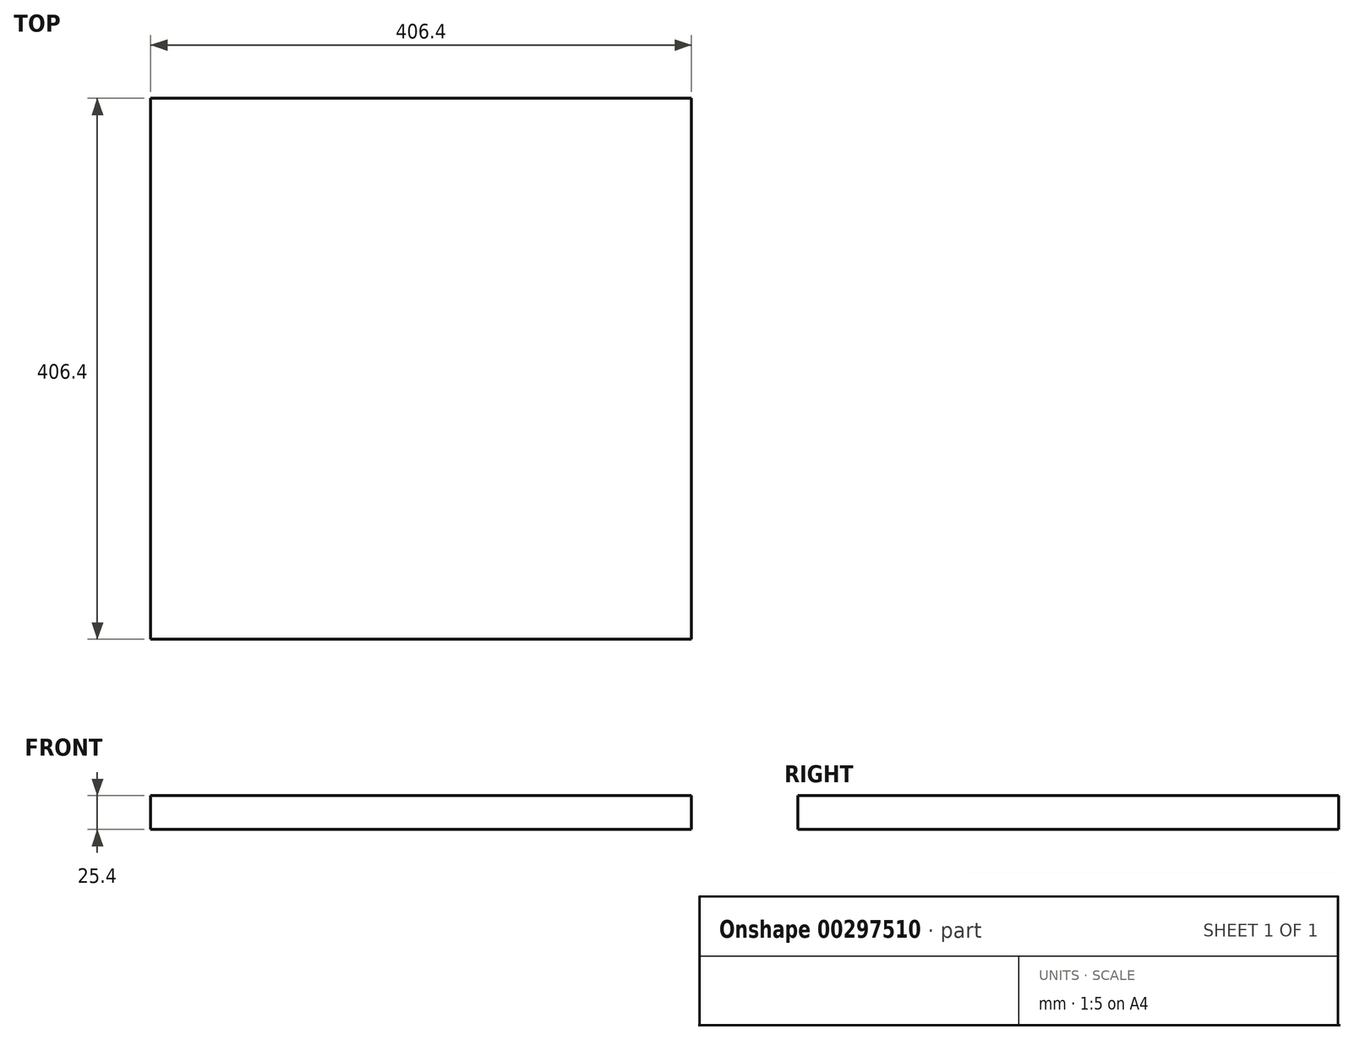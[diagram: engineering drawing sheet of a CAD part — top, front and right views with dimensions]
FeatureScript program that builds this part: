
annotation { "Feature Type Name" : "Feature", "Feature Type Description" : "" }
export const myFeature = defineFeature(function(context is Context, id is Id, definition is map)
    precondition{}
    {
        {
            var Q0;
            Q0=qCreatedBy(makeId("Top.planeOp"),FACE);
            var sketch = newSketch(context, id + "F0", { "sketchPlane" : qUnion([Q0])});
            skLineSegment(sketch, "E0.bottom", {"start": v(0, 0) * mm, "end": v(406.4, 0) * mm});
            skLineSegment(sketch, "E0.top", {"start": v(0, 406.4) * mm, "end": v(406.4, 406.4) * mm});
            skLineSegment(sketch, "E0.left", {"start": v(0, 0) * mm, "end": v(0, 406.4) * mm});
            skLineSegment(sketch, "E0.right", {"start": v(406.4, 0) * mm, "end": v(406.4, 406.4) * mm});
            skSolve(sketch);
        }
        {
            var Q0;
            Q0=makeQuery(id+"F0.imprint","IMPRINT",FACE,{"disambiguationData":[TD([[makeQuery(id+"F0.imprint","IMPRINT",EDGE,{"derivedFrom":sQuery(id+"F0.wireOp",EDGE,"E0.bottom")}),1.0]])]});
            extrude(context, id + "F1", {"entities" : qUnion([Q0]), "depth" : 25.4 * mm});
        }
    });
